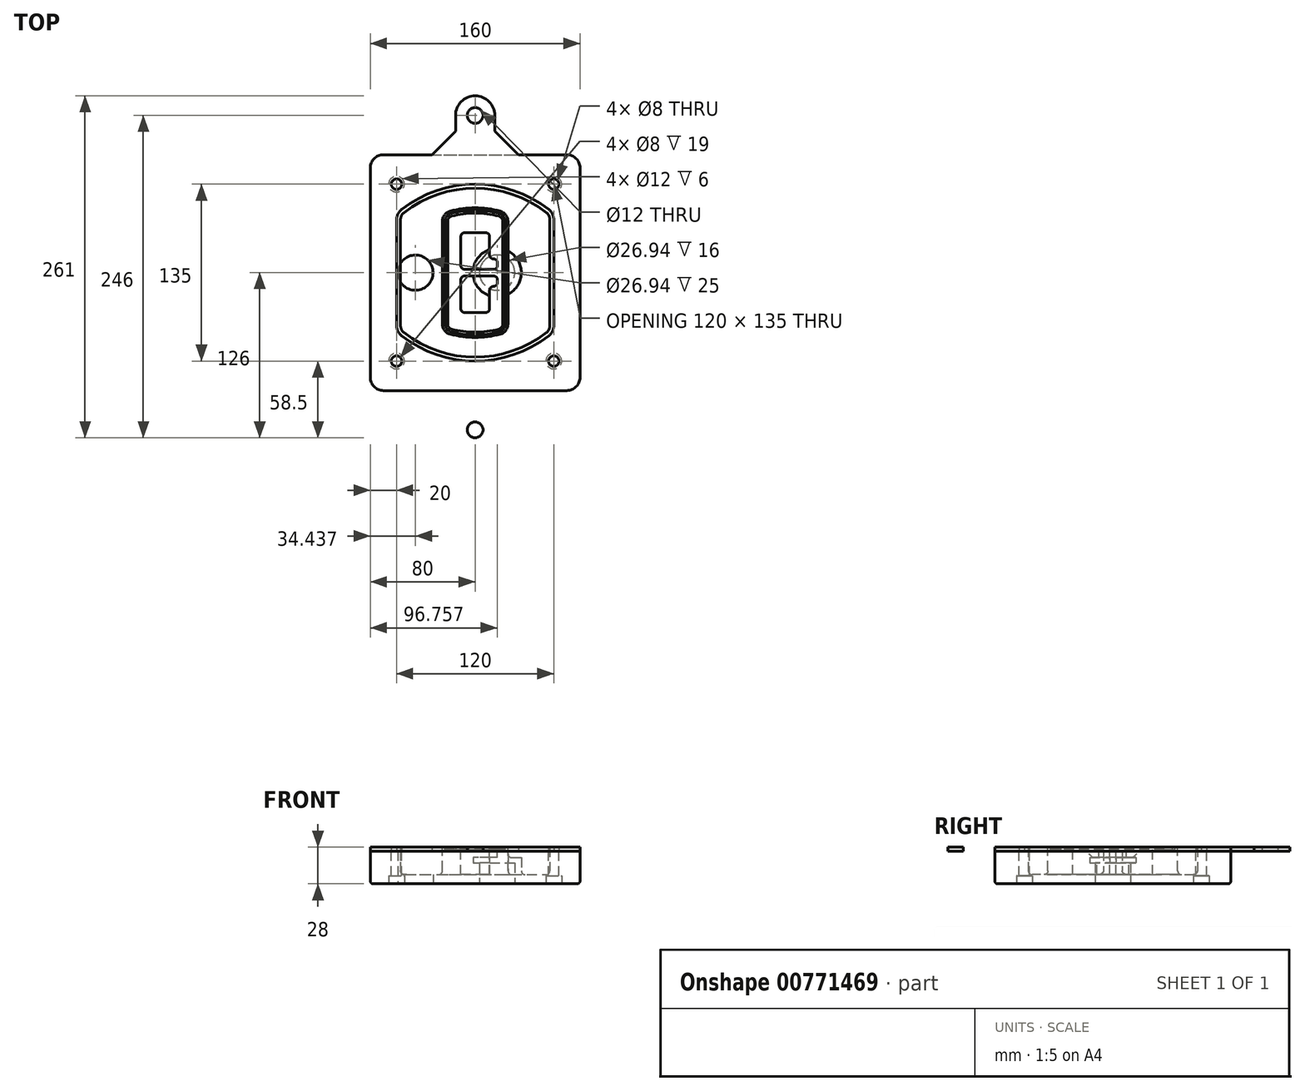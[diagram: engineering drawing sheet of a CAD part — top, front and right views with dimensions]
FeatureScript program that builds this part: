
annotation { "Feature Type Name" : "Feature", "Feature Type Description" : "" }
export const myFeature = defineFeature(function(context is Context, id is Id, definition is map)
    precondition{}
    {
        {
            var Q0;
            Q0=qCreatedBy(makeId("Top.planeOp"),FACE);
            var sketch = newSketch(context, id + "F0", { "sketchPlane" : qUnion([Q0])});
            skPoint(sketch, "E0.rect.middle", {"position": v(0, 0) * mm});
            skLineSegment(sketch, "E1.bottom", {"start": v(-70, -90) * mm, "end": v(70, -90) * mm});
            skLineSegment(sketch, "E1.top", {"start": v(-70, 90) * mm, "end": v(70, 90) * mm});
            skLineSegment(sketch, "E1.left", {"start": v(-80, -80) * mm, "end": v(-80, 80) * mm});
            skLineSegment(sketch, "E1.right", {"start": v(80, -80) * mm, "end": v(80, 80) * mm});
            skLineSegment(sketch, "E2", {"start": v(-80, 90) * mm, "end": v(80, -90) * mm, "construction": true});
            skLineSegment(sketch, "E3", {"start": v(80, 90) * mm, "end": v(-80, -90) * mm, "construction": true});
            skCircle(sketch, "E4", {"center": v(-60, 67.5) * mm, "radius": 4 * mm});
            skCircle(sketch, "E5", {"center": v(60, 67.5) * mm, "radius": 4 * mm});
            skCircle(sketch, "E6", {"center": v(60, -67.5) * mm, "radius": 4 * mm});
            skCircle(sketch, "E7", {"center": v(-60, -67.5) * mm, "radius": 4 * mm});
            skLineSegment(sketch, "E8", {"start": v(-60, 67.5) * mm, "end": v(60, 67.5) * mm, "construction": true});
            skLineSegment(sketch, "E9", {"start": v(60, 67.5) * mm, "end": v(60, -67.5) * mm, "construction": true});
            skLineSegment(sketch, "E10", {"start": v(60, -67.5) * mm, "end": v(-60, -67.5) * mm, "construction": true});
            skLineSegment(sketch, "E11", {"start": v(-60, -67.5) * mm, "end": v(-60, 67.5) * mm, "construction": true});
            skLineSegment(sketch, "E12", {"start": v(-60, 40.3) * mm, "end": v(-60, -40.3) * mm});
            skLineSegment(sketch, "E13", {"start": v(60, 40.3) * mm, "end": v(60, -40.3) * mm});
            skArc(sketch, "E14", {"start": v(56.15, 48.18) * mm, "mid": v(0, 67.5) * mm, "end": v(-56.15, 48.18) * mm});
            skArc(sketch, "E15", {"start": v(-56.15, -48.18) * mm, "mid": v(0, -67.5) * mm, "end": v(56.15, -48.18) * mm});
            skLineSegment(sketch, "E16", {"start": v(-60, 0) * mm, "end": v(60, 0) * mm, "construction": true});
            skPoint(sketch, "E17.visualSharp", {"position": v(-60, -45) * mm});
            skArc(sketch, "E17.filletArc", {"start": v(-60, -40.3) * mm, "mid": v(-58.99, -44.68) * mm, "end": v(-56.15, -48.18) * mm});
            skPoint(sketch, "E18.visualSharp", {"position": v(-60, 45) * mm});
            skArc(sketch, "E18.filletArc", {"start": v(-56.15, 48.18) * mm, "mid": v(-58.99, 44.68) * mm, "end": v(-60, 40.3) * mm});
            skPoint(sketch, "E19.visualSharp", {"position": v(60, 45) * mm});
            skArc(sketch, "E19.filletArc", {"start": v(60, 40.3) * mm, "mid": v(58.99, 44.68) * mm, "end": v(56.15, 48.18) * mm});
            skPoint(sketch, "E20.visualSharp", {"position": v(60, -45) * mm});
            skArc(sketch, "E20.filletArc", {"start": v(56.15, -48.18) * mm, "mid": v(58.99, -44.68) * mm, "end": v(60, -40.3) * mm});
            skPoint(sketch, "E21.visualSharp", {"position": v(-80, 90) * mm});
            skArc(sketch, "E21.filletArc", {"start": v(-70, 90) * mm, "mid": v(-77.07, 87.07) * mm, "end": v(-80, 80) * mm});
            skPoint(sketch, "E22.visualSharp", {"position": v(80, 90) * mm});
            skArc(sketch, "E22.filletArc", {"start": v(80, 80) * mm, "mid": v(77.07, 87.07) * mm, "end": v(70, 90) * mm});
            skPoint(sketch, "E23.visualSharp", {"position": v(80, -90) * mm});
            skArc(sketch, "E23.filletArc", {"start": v(70, -90) * mm, "mid": v(77.07, -87.07) * mm, "end": v(80, -80) * mm});
            skPoint(sketch, "E24.visualSharp", {"position": v(-80, -90) * mm});
            skArc(sketch, "E24.filletArc", {"start": v(-80, -80) * mm, "mid": v(-77.07, -87.07) * mm, "end": v(-70, -90) * mm});
            skArc(sketch, "E25.0", {"start": v(57, 40.3) * mm, "mid": v(56.3, 43.36) * mm, "end": v(54.3, 45.81) * mm});
            skLineSegment(sketch, "E25.1", {"start": v(57, 40.3) * mm, "end": v(57, -40.3) * mm});
            skArc(sketch, "E25.2", {"start": v(54.3, -45.81) * mm, "mid": v(56.3, -43.36) * mm, "end": v(57, -40.3) * mm});
            skArc(sketch, "E25.3", {"start": v(-54.3, -45.81) * mm, "mid": v(0, -64.5) * mm, "end": v(54.3, -45.81) * mm});
            skArc(sketch, "E25.4", {"start": v(-57, -40.3) * mm, "mid": v(-56.3, -43.36) * mm, "end": v(-54.3, -45.81) * mm});
            skArc(sketch, "E25.5", {"start": v(54.3, 45.81) * mm, "mid": v(0, 64.5) * mm, "end": v(-54.3, 45.81) * mm});
            skLineSegment(sketch, "E25.6", {"start": v(-57, 40.3) * mm, "end": v(-57, -40.3) * mm});
            skArc(sketch, "E25.7", {"start": v(-54.3, 45.81) * mm, "mid": v(-56.3, 43.36) * mm, "end": v(-57, 40.3) * mm});
            skArc(sketch, "E26.0", {"start": v(-58.62, 51.33) * mm, "mid": v(-62.58, 46.43) * mm, "end": v(-64, 40.3) * mm});
            skArc(sketch, "E26.1", {"start": v(58.62, 51.33) * mm, "mid": v(0, 71.5) * mm, "end": v(-58.62, 51.33) * mm});
            skArc(sketch, "E26.2", {"start": v(64, 40.3) * mm, "mid": v(62.58, 46.43) * mm, "end": v(58.62, 51.33) * mm});
            skLineSegment(sketch, "E26.3", {"start": v(64, 40.3) * mm, "end": v(64, -40.3) * mm});
            skArc(sketch, "E26.4", {"start": v(58.62, -51.33) * mm, "mid": v(62.58, -46.43) * mm, "end": v(64, -40.3) * mm});
            skLineSegment(sketch, "E26.5", {"start": v(-64, 40.3) * mm, "end": v(-64, -40.3) * mm});
            skArc(sketch, "E26.6", {"start": v(-58.62, -51.33) * mm, "mid": v(0, -71.5) * mm, "end": v(58.62, -51.33) * mm});
            skArc(sketch, "E26.7", {"start": v(-64, -40.3) * mm, "mid": v(-62.58, -46.43) * mm, "end": v(-58.62, -51.33) * mm});
            skSolve(sketch);
        }
        {
            var Q0;
            Q0=makeQuery(id+"F0.imprint","IMPRINT",FACE,{"disambiguationData":[TD([[makeQuery(id+"F0.imprint","IMPRINT",EDGE,{"derivedFrom":sQuery(id+"F0.wireOp",EDGE,"E1.bottom")}),1.0]])]});
            var Q1;
            Q1=makeQuery(id+"F0.imprint","IMPRINT",FACE,{"disambiguationData":[TD([[makeQuery(id+"F0.imprint","IMPRINT",EDGE,{"derivedFrom":sQuery(id+"F0.wireOp",EDGE,"E12")}),1.0]])]});
            var Q2;
            Q2=makeQuery(id+"F0.imprint","IMPRINT",FACE,{"disambiguationData":[TD([[makeQuery(id+"F0.imprint","IMPRINT",EDGE,{"derivedFrom":sQuery(id+"F0.wireOp",EDGE,"E25.0")}),1.0]])]});
            var Q3;
            Q3=makeQuery(id+"F0.imprint","IMPRINT",FACE,{"disambiguationData":[TD([[makeQuery(id+"F0.imprint","IMPRINT",EDGE,{"derivedFrom":sQuery(id+"F0.wireOp",EDGE,"E12")}),-1.0]])]});
            extrude(context, id + "F1", {"entities" : qUnion([Q0, Q1, Q2, Q3]), "oppositeDirection" : true, "depth" : 25 * mm});
        }
        {
            var Q0;
            Q0=makeQuery(id+"F0.imprint","IMPRINT",FACE,{"disambiguationData":[TD([[makeQuery(id+"F0.imprint","IMPRINT",EDGE,{"derivedFrom":sQuery(id+"F0.wireOp",EDGE,"E12")}),1.0]])]});
            extrude(context, id + "F2", {"entities" : qUnion([Q0]), "operationType" : NewBodyOperationType.ADD, "depth" : 3 * mm});
        }
        {
            var Q0;
            Q0=makeQuery(id+"F0.imprint","IMPRINT",FACE,{"disambiguationData":[TD([[makeQuery(id+"F0.imprint","IMPRINT",EDGE,{"derivedFrom":sQuery(id+"F0.wireOp",EDGE,"E25.0")}),1.0]])]});
            extrude(context, id + "F3", {"entities" : qUnion([Q0]), "operationType" : NewBodyOperationType.REMOVE, "oppositeDirection" : true, "depth" : 18 * mm});
        }
        {
            var Q0;
            Q0=makeQuery(id+"F2.opExtrude","CAP_FACE",FACE,{"disambiguationData":[OSD([sQuery(id+"F0.wireOp",EDGE,"E12"),sQuery(id+"F0.wireOp",EDGE,"E13"),sQuery(id+"F0.wireOp",EDGE,"E14"),sQuery(id+"F0.wireOp",EDGE,"E15"),sQuery(id+"F0.wireOp",EDGE,"E17.filletArc"),sQuery(id+"F0.wireOp",EDGE,"E18.filletArc"),sQuery(id+"F0.wireOp",EDGE,"E19.filletArc"),sQuery(id+"F0.wireOp",EDGE,"E20.filletArc"),sQuery(id+"F0.wireOp",EDGE,"E25.0"),sQuery(id+"F0.wireOp",EDGE,"E25.1"),sQuery(id+"F0.wireOp",EDGE,"E25.2"),sQuery(id+"F0.wireOp",EDGE,"E25.3"),sQuery(id+"F0.wireOp",EDGE,"E25.4"),sQuery(id+"F0.wireOp",EDGE,"E25.5"),sQuery(id+"F0.wireOp",EDGE,"E25.6"),sQuery(id+"F0.wireOp",EDGE,"E25.7")])],"isStart":false});
            var sketch = newSketch(context, id + "F4", { "sketchPlane" : qUnion([Q0])});
            skArc(sketch, "E27.0", {"start": v(-19.08, -46.97) * mm, "mid": v(0, -49.5) * mm, "end": v(19.08, -46.97) * mm});
            skArc(sketch, "E28.0", {"start": v(19.08, 46.97) * mm, "mid": v(0, 49.5) * mm, "end": v(-19.08, 46.97) * mm});
            skLineSegment(sketch, "E29", {"start": v(-25, 39.25) * mm, "end": v(-25, -39.25) * mm});
            skLineSegment(sketch, "E30", {"start": v(25, 39.25) * mm, "end": v(25, -39.25) * mm});
            skLineSegment(sketch, "E31", {"start": v(-25, 45.1) * mm, "end": v(25, 45.1) * mm, "construction": true});
            skLineSegment(sketch, "E32", {"start": v(-25, -45.1) * mm, "end": v(25, -45.1) * mm, "construction": true});
            skPoint(sketch, "E33.visualSharp", {"position": v(-25, 45.1) * mm});
            skArc(sketch, "E33.filletArc", {"start": v(-19.08, 46.97) * mm, "mid": v(-23.35, 44.11) * mm, "end": v(-25, 39.25) * mm});
            skPoint(sketch, "E34.visualSharp", {"position": v(25, 45.1) * mm});
            skArc(sketch, "E34.filletArc", {"start": v(25, 39.25) * mm, "mid": v(23.35, 44.11) * mm, "end": v(19.08, 46.97) * mm});
            skPoint(sketch, "E35.visualSharp", {"position": v(25, -45.1) * mm});
            skArc(sketch, "E35.filletArc", {"start": v(19.08, -46.97) * mm, "mid": v(23.35, -44.11) * mm, "end": v(25, -39.25) * mm});
            skPoint(sketch, "E36.visualSharp", {"position": v(-25, -45.1) * mm});
            skArc(sketch, "E36.filletArc", {"start": v(-25, -39.25) * mm, "mid": v(-23.35, -44.11) * mm, "end": v(-19.08, -46.97) * mm});
            skArc(sketch, "E37.0", {"start": v(54.3, 45.81) * mm, "mid": v(0, 64.5) * mm, "end": v(-54.3, 45.81) * mm});
            skArc(sketch, "E37.1", {"start": v(-54.3, 45.81) * mm, "mid": v(-56.3, 43.36) * mm, "end": v(-57, 40.3) * mm});
            skLineSegment(sketch, "E37.2", {"start": v(-57, 40.3) * mm, "end": v(-57, -40.3) * mm});
            skArc(sketch, "E37.3", {"start": v(-57, -40.3) * mm, "mid": v(-56.3, -43.36) * mm, "end": v(-54.3, -45.81) * mm});
            skArc(sketch, "E37.4", {"start": v(-54.3, -45.81) * mm, "mid": v(0, -64.5) * mm, "end": v(54.3, -45.81) * mm});
            skArc(sketch, "E37.5", {"start": v(54.3, -45.81) * mm, "mid": v(56.3, -43.36) * mm, "end": v(57, -40.3) * mm});
            skLineSegment(sketch, "E37.6", {"start": v(57, 40.3) * mm, "end": v(57, -40.3) * mm});
            skArc(sketch, "E37.7", {"start": v(57, 40.3) * mm, "mid": v(56.3, 43.36) * mm, "end": v(54.3, 45.81) * mm});
            skLineSegment(sketch, "E38.0", {"start": v(23, 39.25) * mm, "end": v(23, -39.25) * mm});
            skArc(sketch, "E38.1", {"start": v(18.56, -45.04) * mm, "mid": v(21.76, -42.9) * mm, "end": v(23, -39.25) * mm});
            skArc(sketch, "E38.2", {"start": v(-18.56, -45.04) * mm, "mid": v(0, -47.5) * mm, "end": v(18.56, -45.04) * mm});
            skArc(sketch, "E38.3", {"start": v(-23, -39.25) * mm, "mid": v(-21.76, -42.9) * mm, "end": v(-18.56, -45.04) * mm});
            skLineSegment(sketch, "E38.4", {"start": v(-23, 39.25) * mm, "end": v(-23, -39.25) * mm});
            skArc(sketch, "E38.5", {"start": v(23, 39.25) * mm, "mid": v(21.76, 42.9) * mm, "end": v(18.56, 45.04) * mm});
            skArc(sketch, "E38.6", {"start": v(-18.56, 45.04) * mm, "mid": v(-21.76, 42.9) * mm, "end": v(-23, 39.25) * mm});
            skArc(sketch, "E38.7", {"start": v(18.56, 45.04) * mm, "mid": v(0, 47.5) * mm, "end": v(-18.56, 45.04) * mm});
            skArc(sketch, "E39.0", {"start": v(21, 39.25) * mm, "mid": v(20.18, 41.68) * mm, "end": v(18.04, 43.1) * mm});
            skLineSegment(sketch, "E39.1", {"start": v(21, 39.25) * mm, "end": v(21, -39.25) * mm});
            skArc(sketch, "E39.2", {"start": v(18.04, -43.1) * mm, "mid": v(20.18, -41.68) * mm, "end": v(21, -39.25) * mm});
            skArc(sketch, "E39.3", {"start": v(-18.04, -43.1) * mm, "mid": v(0, -45.5) * mm, "end": v(18.04, -43.1) * mm});
            skArc(sketch, "E39.4", {"start": v(-21, -39.25) * mm, "mid": v(-20.18, -41.68) * mm, "end": v(-18.04, -43.1) * mm});
            skArc(sketch, "E39.5", {"start": v(18.04, 43.1) * mm, "mid": v(0, 45.5) * mm, "end": v(-18.04, 43.1) * mm});
            skLineSegment(sketch, "E39.6", {"start": v(-21, 39.25) * mm, "end": v(-21, -39.25) * mm});
            skArc(sketch, "E39.7", {"start": v(-18.04, 43.1) * mm, "mid": v(-20.18, 41.68) * mm, "end": v(-21, 39.25) * mm});
            skLineSegment(sketch, "E40", {"start": v(-25, 0) * mm, "end": v(25, 0) * mm, "construction": true});
            skLineSegment(sketch, "E41", {"start": v(-11, 5.5) * mm, "end": v(-11, 27.5) * mm});
            skLineSegment(sketch, "E42", {"start": v(-8, 30.5) * mm, "end": v(8, 30.5) * mm});
            skLineSegment(sketch, "E43", {"start": v(11, 27.5) * mm, "end": v(11, 13.5) * mm});
            skLineSegment(sketch, "E44", {"start": v(14, 10.5) * mm, "end": v(14, 10.5) * mm});
            skLineSegment(sketch, "E45", {"start": v(17, 7.5) * mm, "end": v(17, 5.5) * mm});
            skLineSegment(sketch, "E46", {"start": v(14, 2.5) * mm, "end": v(-8, 2.5) * mm});
            skPoint(sketch, "E47.visualSharp", {"position": v(-11, 30.5) * mm});
            skArc(sketch, "E47.filletArc", {"start": v(-8, 30.5) * mm, "mid": v(-10.12, 29.62) * mm, "end": v(-11, 27.5) * mm});
            skPoint(sketch, "E48.visualSharp", {"position": v(11, 30.5) * mm});
            skArc(sketch, "E48.filletArc", {"start": v(11, 27.5) * mm, "mid": v(10.12, 29.62) * mm, "end": v(8, 30.5) * mm});
            skPoint(sketch, "E49.visualSharp", {"position": v(11, 10.5) * mm});
            skArc(sketch, "E49.filletArc", {"start": v(11, 13.5) * mm, "mid": v(11.88, 11.38) * mm, "end": v(14, 10.5) * mm});
            skPoint(sketch, "E50.visualSharp", {"position": v(17, 10.5) * mm});
            skArc(sketch, "E50.filletArc", {"start": v(17, 7.5) * mm, "mid": v(16.12, 9.62) * mm, "end": v(14, 10.5) * mm});
            skPoint(sketch, "E51.visualSharp", {"position": v(17, 2.5) * mm});
            skArc(sketch, "E51.filletArc", {"start": v(14, 2.5) * mm, "mid": v(16.12, 3.38) * mm, "end": v(17, 5.5) * mm});
            skPoint(sketch, "E52.visualSharp", {"position": v(-11, 2.5) * mm});
            skArc(sketch, "E52.filletArc", {"start": v(-11, 5.5) * mm, "mid": v(-10.12, 3.38) * mm, "end": v(-8, 2.5) * mm});
            skLineSegment(sketch, "E53.0.MirrorCS", {"start": v(14, -2.5) * mm, "end": v(-8, -2.5) * mm});
            skArc(sketch, "E54.0.MirrorCS", {"start": v(-11, -5.5) * mm, "mid": v(-10.12, -3.38) * mm, "end": v(-8, -2.5) * mm});
            skLineSegment(sketch, "E55.0.MirrorCS", {"start": v(-11, -5.5) * mm, "end": v(-11, -27.5) * mm});
            skArc(sketch, "E56.0.MirrorCS", {"start": v(-8, -30.5) * mm, "mid": v(-10.12, -29.62) * mm, "end": v(-11, -27.5) * mm});
            skLineSegment(sketch, "E57.0.MirrorCS", {"start": v(-8, -30.5) * mm, "end": v(8, -30.5) * mm});
            skArc(sketch, "E58.0.MirrorCS", {"start": v(11, -27.5) * mm, "mid": v(10.12, -29.62) * mm, "end": v(8, -30.5) * mm});
            skLineSegment(sketch, "E59.0.MirrorCS", {"start": v(11, -27.5) * mm, "end": v(11, -13.5) * mm});
            skArc(sketch, "E60.0.MirrorCS", {"start": v(11, -13.5) * mm, "mid": v(11.88, -11.38) * mm, "end": v(14, -10.5) * mm});
            skArc(sketch, "E61.0.MirrorCS", {"start": v(17, -7.5) * mm, "mid": v(16.12, -9.62) * mm, "end": v(14, -10.5) * mm});
            skLineSegment(sketch, "E62.0.MirrorCS", {"start": v(17, -7.5) * mm, "end": v(17, -5.5) * mm});
            skArc(sketch, "E63.0.MirrorCS", {"start": v(14, -2.5) * mm, "mid": v(16.12, -3.38) * mm, "end": v(17, -5.5) * mm});
            skSolve(sketch);
        }
        {
            var Q0;
            Q0=makeQuery(id+"F4.imprint","IMPRINT",FACE,{"disambiguationData":[TD([[makeQuery(id+"F4.imprint","IMPRINT",EDGE,{"derivedFrom":sQuery(id+"F4.wireOp",EDGE,"E27.0")}),1.0]])]});
            var Q1;
            Q1=makeQuery(id+"F4.imprint","IMPRINT",FACE,{"disambiguationData":[TD([[makeQuery(id+"F4.imprint","IMPRINT",EDGE,{"derivedFrom":sQuery(id+"F4.wireOp",EDGE,"E38.0")}),-1.0]])]});
            var Q2;
            Q2=makeQuery(id+"F4.imprint","IMPRINT",FACE,{"disambiguationData":[TD([[makeQuery(id+"F4.imprint","IMPRINT",EDGE,{"derivedFrom":sQuery(id+"F4.wireOp",EDGE,"E39.0")}),1.0]])]});
            extrude(context, id + "F5", {"entities" : qUnion([Q0, Q1, Q2]), "operationType" : NewBodyOperationType.ADD, "endBound" : BoundingType.UP_TO_NEXT, "oppositeDirection" : true, "depth" : 25 * mm});
        }
        {
            var Q0;
            Q0=makeQuery(id+"F4.imprint","IMPRINT",FACE,{"disambiguationData":[TD([[makeQuery(id+"F4.imprint","IMPRINT",EDGE,{"derivedFrom":sQuery(id+"F4.wireOp",EDGE,"E38.0")}),-1.0]])]});
            extrude(context, id + "F6", {"entities" : qUnion([Q0]), "operationType" : NewBodyOperationType.REMOVE, "oppositeDirection" : true, "depth" : 2 * mm});
        }
        {
            var Q0;
            Q0=makeQuery(id+"F1.opExtrude","CAP_FACE",FACE,{"disambiguationData":[OSD([sQuery(id+"F0.wireOp",EDGE,"E1.bottom"),sQuery(id+"F0.wireOp",EDGE,"E1.top"),sQuery(id+"F0.wireOp",EDGE,"E1.left"),sQuery(id+"F0.wireOp",EDGE,"E1.right"),sQuery(id+"F0.wireOp",EDGE,"E4"),sQuery(id+"F0.wireOp",EDGE,"E5"),sQuery(id+"F0.wireOp",EDGE,"E6"),sQuery(id+"F0.wireOp",EDGE,"E7"),sQuery(id+"F0.wireOp",EDGE,"E21.filletArc"),sQuery(id+"F0.wireOp",EDGE,"E22.filletArc"),sQuery(id+"F0.wireOp",EDGE,"E23.filletArc"),sQuery(id+"F0.wireOp",EDGE,"E24.filletArc")])],"isStart":false});
            var sketch = newSketch(context, id + "F7", { "sketchPlane" : qUnion([Q0])});
            skCircle(sketch, "E64", {"center": v(16.76, 0) * mm, "radius": 13.47 * mm});
            skCircle(sketch, "E65", {"center": v(-45.56, 0) * mm, "radius": 13.47 * mm});
            skLineSegment(sketch, "E66", {"start": v(80, 0) * mm, "end": v(-80, 0) * mm});
            skCircle(sketch, "E67", {"center": v(16.76, 0) * mm, "radius": 18.47 * mm});
            skCircle(sketch, "E68", {"center": v(60, -67.5) * mm, "radius": 6 * mm});
            skCircle(sketch, "E69", {"center": v(-60, -67.5) * mm, "radius": 6 * mm});
            skCircle(sketch, "E70", {"center": v(-60, 67.5) * mm, "radius": 6 * mm});
            skCircle(sketch, "E71", {"center": v(60, 67.5) * mm, "radius": 6 * mm});
            skSolve(sketch);
        }
        {
            var Q0;
            {var subQ1=sQuery(id+"F7.wireOp",EDGE,"E66");var subQ4=sQuery(id+"F7.wireOp",EDGE,"E64");var subQ6=makeQuery(id+"F7.imprint","INTERSECT",VERTEX,{"disambiguationData":[OD(0.0)],"derivedFrom":[subQ4,subQ1]});Q0=makeQuery(id+"F7.imprint","IMPRINT",FACE,{"disambiguationData":[TD([[makeQuery(id+"F7.imprint","IMPRINT",EDGE,{"disambiguationData":[TD([[subQ6,-1.0]])],"derivedFrom":subQ4}),-1.0]])]});}
            var Q1;
            {var subQ0=sQuery(id+"F7.wireOp",EDGE,"E66");var subQ1=sQuery(id+"F7.wireOp",EDGE,"E64");var subQ3=makeQuery(id+"F7.imprint","INTERSECT",VERTEX,{"disambiguationData":[OD(0.0)],"derivedFrom":[subQ1,subQ0]});Q1=makeQuery(id+"F7.imprint","IMPRINT",FACE,{"disambiguationData":[TD([[makeQuery(id+"F7.imprint","IMPRINT",EDGE,{"disambiguationData":[TD([[subQ3,-1.0]])],"derivedFrom":subQ1}),1.0]])]});}
            var Q2;
            {var subQ0=sQuery(id+"F7.wireOp",EDGE,"E66");var subQ1=sQuery(id+"F7.wireOp",EDGE,"E64");var subQ3=makeQuery(id+"F7.imprint","INTERSECT",VERTEX,{"disambiguationData":[OD(0.0)],"derivedFrom":[subQ1,subQ0]});Q2=makeQuery(id+"F7.imprint","IMPRINT",FACE,{"disambiguationData":[TD([[makeQuery(id+"F7.imprint","IMPRINT",EDGE,{"disambiguationData":[TD([[subQ3,1.0]])],"derivedFrom":subQ1}),1.0]])]});}
            var Q3;
            {var subQ1=sQuery(id+"F7.wireOp",EDGE,"E66");var subQ4=sQuery(id+"F7.wireOp",EDGE,"E64");var subQ6=makeQuery(id+"F7.imprint","INTERSECT",VERTEX,{"disambiguationData":[OD(0.0)],"derivedFrom":[subQ4,subQ1]});Q3=makeQuery(id+"F7.imprint","IMPRINT",FACE,{"disambiguationData":[TD([[makeQuery(id+"F7.imprint","IMPRINT",EDGE,{"disambiguationData":[TD([[subQ6,1.0]])],"derivedFrom":subQ4}),-1.0]])]});}
            extrude(context, id + "F8", {"entities" : qUnion([Q0, Q1, Q2, Q3]), "operationType" : NewBodyOperationType.ADD, "oppositeDirection" : true, "depth" : 20 * mm});
        }
        {
            var Q0;
            {var subQ0=sQuery(id+"F7.wireOp",EDGE,"E66");var subQ1=sQuery(id+"F7.wireOp",EDGE,"E64");var subQ3=makeQuery(id+"F7.imprint","INTERSECT",VERTEX,{"disambiguationData":[OD(0.0)],"derivedFrom":[subQ1,subQ0]});Q0=makeQuery(id+"F7.imprint","IMPRINT",FACE,{"disambiguationData":[TD([[makeQuery(id+"F7.imprint","IMPRINT",EDGE,{"disambiguationData":[TD([[subQ3,-1.0]])],"derivedFrom":subQ1}),1.0]])]});}
            var Q1;
            {var subQ0=sQuery(id+"F7.wireOp",EDGE,"E66");var subQ1=sQuery(id+"F7.wireOp",EDGE,"E64");var subQ3=makeQuery(id+"F7.imprint","INTERSECT",VERTEX,{"disambiguationData":[OD(0.0)],"derivedFrom":[subQ1,subQ0]});Q1=makeQuery(id+"F7.imprint","IMPRINT",FACE,{"disambiguationData":[TD([[makeQuery(id+"F7.imprint","IMPRINT",EDGE,{"disambiguationData":[TD([[subQ3,1.0]])],"derivedFrom":subQ1}),1.0]])]});}
            extrude(context, id + "F9", {"entities" : qUnion([Q0, Q1]), "operationType" : NewBodyOperationType.REMOVE, "oppositeDirection" : true, "depth" : 16 * mm});
        }
        {
            var Q0;
            {var subQ0=sQuery(id+"F7.wireOp",EDGE,"E66");var subQ1=sQuery(id+"F7.wireOp",EDGE,"E65");var subQ3=makeQuery(id+"F7.imprint","INTERSECT",VERTEX,{"disambiguationData":[OD(0.0)],"derivedFrom":[subQ1,subQ0]});Q0=makeQuery(id+"F7.imprint","IMPRINT",FACE,{"disambiguationData":[TD([[makeQuery(id+"F7.imprint","IMPRINT",EDGE,{"disambiguationData":[TD([[subQ3,-1.0]])],"derivedFrom":subQ1}),1.0]])]});}
            var Q1;
            {var subQ0=sQuery(id+"F7.wireOp",EDGE,"E66");var subQ1=sQuery(id+"F7.wireOp",EDGE,"E65");var subQ3=makeQuery(id+"F7.imprint","INTERSECT",VERTEX,{"disambiguationData":[OD(0.0)],"derivedFrom":[subQ1,subQ0]});Q1=makeQuery(id+"F7.imprint","IMPRINT",FACE,{"disambiguationData":[TD([[makeQuery(id+"F7.imprint","IMPRINT",EDGE,{"disambiguationData":[TD([[subQ3,1.0]])],"derivedFrom":subQ1}),1.0]])]});}
            extrude(context, id + "F10", {"entities" : qUnion([Q0, Q1]), "operationType" : NewBodyOperationType.REMOVE, "oppositeDirection" : true, "depth" : 25 * mm});
        }
        {
            var Q0;
            Q0=makeQuery(id+"F7.imprint","IMPRINT",FACE,{"disambiguationData":[TD([[makeQuery(id+"F7.imprint","IMPRINT",EDGE,{"derivedFrom":sQuery(id+"F7.wireOp",EDGE,"E68")}),1.0]])]});
            var Q1;
            Q1=makeQuery(id+"F7.imprint","IMPRINT",FACE,{"disambiguationData":[TD([[makeQuery(id+"F7.imprint","IMPRINT",EDGE,{"derivedFrom":makeQuery(id+"F1.opExtrude","CAP_EDGE",EDGE,{"disambiguationData":[OSD([sQuery(id+"F0.wireOp",EDGE,"E5")])],"isStart":false})}),-1.0]])]});
            var Q2;
            Q2=makeQuery(id+"F7.imprint","IMPRINT",FACE,{"disambiguationData":[TD([[makeQuery(id+"F7.imprint","IMPRINT",EDGE,{"derivedFrom":sQuery(id+"F7.wireOp",EDGE,"E69")}),1.0]])]});
            var Q3;
            Q3=makeQuery(id+"F7.imprint","IMPRINT",FACE,{"disambiguationData":[TD([[makeQuery(id+"F7.imprint","IMPRINT",EDGE,{"derivedFrom":makeQuery(id+"F1.opExtrude","CAP_EDGE",EDGE,{"disambiguationData":[OSD([sQuery(id+"F0.wireOp",EDGE,"E4")])],"isStart":false})}),-1.0]])]});
            var Q4;
            Q4=makeQuery(id+"F7.imprint","IMPRINT",FACE,{"disambiguationData":[TD([[makeQuery(id+"F7.imprint","IMPRINT",EDGE,{"derivedFrom":sQuery(id+"F7.wireOp",EDGE,"E70")}),1.0]])]});
            var Q5;
            Q5=makeQuery(id+"F7.imprint","IMPRINT",FACE,{"disambiguationData":[TD([[makeQuery(id+"F7.imprint","IMPRINT",EDGE,{"derivedFrom":makeQuery(id+"F1.opExtrude","CAP_EDGE",EDGE,{"disambiguationData":[OSD([sQuery(id+"F0.wireOp",EDGE,"E7")])],"isStart":false})}),-1.0]])]});
            var Q6;
            Q6=makeQuery(id+"F7.imprint","IMPRINT",FACE,{"disambiguationData":[TD([[makeQuery(id+"F7.imprint","IMPRINT",EDGE,{"derivedFrom":sQuery(id+"F7.wireOp",EDGE,"E71")}),1.0]])]});
            var Q7;
            Q7=makeQuery(id+"F7.imprint","IMPRINT",FACE,{"disambiguationData":[TD([[makeQuery(id+"F7.imprint","IMPRINT",EDGE,{"derivedFrom":makeQuery(id+"F1.opExtrude","CAP_EDGE",EDGE,{"disambiguationData":[OSD([sQuery(id+"F0.wireOp",EDGE,"E6")])],"isStart":false})}),-1.0]])]});
            extrude(context, id + "F11", {"entities" : qUnion([Q0, Q1, Q2, Q3, Q4, Q5, Q6, Q7]), "operationType" : NewBodyOperationType.REMOVE, "oppositeDirection" : true, "depth" : 6 * mm});
        }
        {
            var Q0;
            Q0=makeQuery(id+"F9.boolean.opBoolean","COPY",FACE,{"derivedFrom":makeQuery(id+"F9.opExtrude","CAP_FACE",FACE,{"disambiguationData":[OSD([sQuery(id+"F7.wireOp",EDGE,"E64")])],"isStart":false})});
            var sketch = newSketch(context, id + "F12", { "sketchPlane" : qUnion([Q0])});
            skArc(sketch, "E72.0", {"start": v(11, 17.55) * mm, "mid": v(2.57, 11.82) * mm, "end": v(-1.54, 2.5) * mm});
            skArc(sketch, "E72.1", {"start": v(-1.54, -2.5) * mm, "mid": v(2.57, -11.82) * mm, "end": v(11, -17.55) * mm});
            skLineSegment(sketch, "E73", {"start": v(-1.54, -2.5) * mm, "end": v(14, -2.5) * mm});
            skLineSegment(sketch, "E74.0", {"start": v(14, 2.5) * mm, "end": v(-1.54, 2.5) * mm});
            skArc(sketch, "E74.1", {"start": v(14, 2.5) * mm, "mid": v(16.12, 3.38) * mm, "end": v(17, 5.5) * mm});
            skLineSegment(sketch, "E74.2", {"start": v(17, 7.5) * mm, "end": v(17, 5.5) * mm});
            skArc(sketch, "E74.3", {"start": v(17, 7.5) * mm, "mid": v(16.12, 9.62) * mm, "end": v(14, 10.5) * mm});
            skArc(sketch, "E74.4", {"start": v(11, 13.5) * mm, "mid": v(11.88, 11.38) * mm, "end": v(14, 10.5) * mm});
            skLineSegment(sketch, "E74.5", {"start": v(11, 17.55) * mm, "end": v(11, 13.5) * mm});
            skLineSegment(sketch, "E74.7", {"start": v(14, -2.5) * mm, "end": v(-1.54, -2.5) * mm});
            skArc(sketch, "E74.8", {"start": v(14, -2.5) * mm, "mid": v(16.12, -3.38) * mm, "end": v(17, -5.5) * mm});
            skLineSegment(sketch, "E74.9", {"start": v(17, -7.5) * mm, "end": v(17, -5.5) * mm});
            skArc(sketch, "E74.10", {"start": v(17, -7.5) * mm, "mid": v(16.12, -9.62) * mm, "end": v(14, -10.5) * mm});
            skArc(sketch, "E74.11", {"start": v(11, -13.5) * mm, "mid": v(11.88, -11.38) * mm, "end": v(14, -10.5) * mm});
            skLineSegment(sketch, "E74.12", {"start": v(11, -17.55) * mm, "end": v(11, -13.5) * mm});
            skPoint(sketch, "E75.orphan", {"position": v(11, -27.5) * mm});
            skPoint(sketch, "E76.orphan", {"position": v(-8, -2.5) * mm});
            skPoint(sketch, "E77.orphan", {"position": v(-8, 2.5) * mm});
            skPoint(sketch, "E78.orphan", {"position": v(11, 27.5) * mm});
            skSolve(sketch);
        }
        {
            var Q0;
            {var subQ7=sQuery(id+"F12.wireOp",EDGE,"E72.0");var subQ14=sQuery(id+"F12.wireOp",EDGE,"E72.1");var subQ16=sQuery(id+"F12.wireOp",EDGE,"E74.1");var subQ18=sQuery(id+"F12.wireOp",EDGE,"E74.8");Q0=qUnion([makeQuery(id+"F12.imprint","IMPRINT",FACE,{"disambiguationData":[TD([[makeQuery(id+"F12.imprint","IMPRINT",EDGE,{"derivedFrom":subQ7}),1.0]])]}),makeQuery(id+"F12.imprint","IMPRINT",FACE,{"disambiguationData":[TD([[makeQuery(id+"F12.imprint","IMPRINT",EDGE,{"derivedFrom":subQ14}),1.0]])]}),makeQuery(id+"F12.imprint","IMPRINT",FACE,{"disambiguationData":[TD([[makeQuery(id+"F12.imprint","IMPRINT",EDGE,{"derivedFrom":subQ16}),1.0]])]}),makeQuery(id+"F12.imprint","IMPRINT",FACE,{"disambiguationData":[TD([[makeQuery(id+"F12.imprint","IMPRINT",EDGE,{"derivedFrom":subQ18}),-1.0]])]})]);}
            var Q1;
            Q1=makeQuery(id+"F5.boolean.opBoolean","SPLIT",FACE,{"disambiguationData":[TD([makeQuery(id+"F5.opExtrude","SWEPT_FACE",FACE,{"disambiguationData":[OSD([sQuery(id+"F4.wireOp",EDGE,"E41")])]})])],"derivedFrom":makeQuery(id+"F3.boolean.opBoolean","COPY",FACE,{"derivedFrom":makeQuery(id+"F3.opExtrude","CAP_FACE",FACE,{"disambiguationData":[OSD([sQuery(id+"F0.wireOp",EDGE,"E25.0"),sQuery(id+"F0.wireOp",EDGE,"E25.1"),sQuery(id+"F0.wireOp",EDGE,"E25.2"),sQuery(id+"F0.wireOp",EDGE,"E25.3"),sQuery(id+"F0.wireOp",EDGE,"E25.4"),sQuery(id+"F0.wireOp",EDGE,"E25.5"),sQuery(id+"F0.wireOp",EDGE,"E25.6"),sQuery(id+"F0.wireOp",EDGE,"E25.7")])],"isStart":false})})});
            extrude(context, id + "F13", {"entities" : qUnion([Q0]), "operationType" : NewBodyOperationType.REMOVE, "endBound" : BoundingType.UP_TO_SURFACE, "endBoundEntityFace" : qUnion([Q1]), "depth" : 25 * mm});
        }
        {
            var Q0;
            Q0=makeQuery(id+"F3.boolean.opBoolean","COPY",EDGE,{"derivedFrom":makeQuery(id+"F3.opExtrude","CAP_EDGE",EDGE,{"disambiguationData":[OSD([sQuery(id+"F0.wireOp",EDGE,"E25.6")])],"isStart":false})});
            var Q1;
            Q1=makeQuery(id+"F8.boolean.opBoolean","INTERSECT",EDGE,{"derivedFrom":[makeQuery(id+"F5.opExtrude","SWEPT_FACE",FACE,{"disambiguationData":[OSD([sQuery(id+"F4.wireOp",EDGE,"E30")])]}),makeQuery(id+"F8.opExtrude","CAP_FACE",FACE,{"disambiguationData":[OSD([sQuery(id+"F7.wireOp",EDGE,"E67")])],"isStart":false})]});
            var Q2;
            Q2=makeQuery(id+"F8.boolean.opBoolean","INTERSECT",EDGE,{"disambiguationData":[OD(1.0)],"derivedFrom":[makeQuery(id+"F5.opExtrude","SWEPT_FACE",FACE,{"disambiguationData":[OSD([sQuery(id+"F4.wireOp",EDGE,"E30")])]}),makeQuery(id+"F8.opExtrude","SWEPT_FACE",FACE,{"disambiguationData":[OSD([sQuery(id+"F7.wireOp",EDGE,"E67")])]})]});
            var Q3;
            {var subQ0=sQuery(id+"F4.wireOp",EDGE,"E30");Q3=makeQuery(id+"F8.boolean.opBoolean","SPLIT",EDGE,{"disambiguationData":[TD([makeQuery(id+"F5.opExtrude","SWEPT_FACE",FACE,{"disambiguationData":[OSD([sQuery(id+"F4.wireOp",EDGE,"E35.filletArc")])]})])],"derivedFrom":makeQuery(id+"F5.opExtrude","CAP_EDGE",EDGE,{"disambiguationData":[OSD([subQ0])],"isStart":false})});}
            var Q4;
            {var subQ0=sQuery(id+"F0.wireOp",EDGE,"E25.7");var subQ1=sQuery(id+"F0.wireOp",EDGE,"E25.1");var subQ2=sQuery(id+"F0.wireOp",EDGE,"E25.6");var subQ3=sQuery(id+"F0.wireOp",EDGE,"E25.5");var subQ4=sQuery(id+"F0.wireOp",EDGE,"E25.4");var subQ5=sQuery(id+"F0.wireOp",EDGE,"E25.0");var subQ6=sQuery(id+"F0.wireOp",EDGE,"E25.2");var subQ7=sQuery(id+"F0.wireOp",EDGE,"E25.3");Q4=makeQuery(id+"F8.boolean.opBoolean","INTERSECT",EDGE,{"derivedFrom":[makeQuery(id+"F5.boolean.opBoolean","SPLIT",FACE,{"disambiguationData":[TD([makeQuery(id+"F2.opExtrude","SWEPT_FACE",FACE,{"disambiguationData":[OSD([subQ5])]})])],"derivedFrom":makeQuery(id+"F3.boolean.opBoolean","COPY",FACE,{"derivedFrom":makeQuery(id+"F3.opExtrude","CAP_FACE",FACE,{"disambiguationData":[OSD([subQ5,subQ1,subQ6,subQ7,subQ4,subQ3,subQ2,subQ0])],"isStart":false})})}),makeQuery(id+"F8.opExtrude","SWEPT_FACE",FACE,{"disambiguationData":[OSD([sQuery(id+"F7.wireOp",EDGE,"E67")])]})]});}
            var Q5;
            Q5=makeQuery(id+"F8.boolean.opBoolean","INTERSECT",EDGE,{"disambiguationData":[OD(0.0)],"derivedFrom":[makeQuery(id+"F5.opExtrude","SWEPT_FACE",FACE,{"disambiguationData":[OSD([sQuery(id+"F4.wireOp",EDGE,"E30")])]}),makeQuery(id+"F8.opExtrude","SWEPT_FACE",FACE,{"disambiguationData":[OSD([sQuery(id+"F7.wireOp",EDGE,"E67")])]})]});
            fillet(context, id + "F14", {"entities" : qUnion([Q0, Q1, Q2, Q3, Q4, Q5]), "radius" : 3 * mm, "tangentPropagation" : true, "allowEdgeOverflow" : false});
        }
        {
            var Q0;
            Q0=makeQuery(id+"F1.opExtrude","CAP_EDGE",EDGE,{"disambiguationData":[OSD([sQuery(id+"F0.wireOp",EDGE,"E1.bottom")])],"isStart":false});
            fillet(context, id + "F15", {"entities" : qUnion([Q0]), "radius" : 2 * mm, "tangentPropagation" : true, "allowEdgeOverflow" : false});
        }
        {
            var Q0;
            {var subQ0=sQuery(id+"F0.wireOp",EDGE,"E21.filletArc");var subQ1=sQuery(id+"F0.wireOp",EDGE,"E7");var subQ2=sQuery(id+"F0.wireOp",EDGE,"E6");var subQ3=sQuery(id+"F0.wireOp",EDGE,"E5");var subQ4=sQuery(id+"F0.wireOp",EDGE,"E4");var subQ5=sQuery(id+"F0.wireOp",EDGE,"E22.filletArc");var subQ6=sQuery(id+"F0.wireOp",EDGE,"E1.bottom");var subQ7=sQuery(id+"F0.wireOp",EDGE,"E1.right");var subQ8=sQuery(id+"F0.wireOp",EDGE,"E1.top");var subQ9=sQuery(id+"F0.wireOp",EDGE,"E1.left");var subQ10=sQuery(id+"F0.wireOp",EDGE,"E23.filletArc");var subQ11=sQuery(id+"F0.wireOp",EDGE,"E24.filletArc");Q0=makeQuery(id+"F2.boolean.opBoolean","SPLIT",FACE,{"disambiguationData":[TD([makeQuery(id+"F1.opExtrude","SWEPT_FACE",FACE,{"disambiguationData":[OSD([subQ6])]})])],"derivedFrom":makeQuery(id+"F1.opExtrude","CAP_FACE",FACE,{"disambiguationData":[OSD([subQ6,subQ8,subQ9,subQ7,subQ4,subQ3,subQ2,subQ1,subQ0,subQ5,subQ10,subQ11])],"isStart":true})});}
            var sketch = newSketch(context, id + "F16", { "sketchPlane" : qUnion([Q0])});
            skLineSegment(sketch, "E79", {"start": v(0, 90) * mm, "end": v(0, 120) * mm, "construction": true});
            skCircle(sketch, "E80", {"center": v(0, 120) * mm, "radius": 6 * mm});
            skLineSegment(sketch, "E81", {"start": v(-15, 120) * mm, "end": v(-15, 108) * mm});
            skLineSegment(sketch, "E82", {"start": v(15, 120) * mm, "end": v(15, 108) * mm});
            skLineSegment(sketch, "E83", {"start": v(15, 108) * mm, "end": v(33, 90) * mm});
            skLineSegment(sketch, "E84", {"start": v(-15, 108) * mm, "end": v(-33, 90) * mm});
            skArc(sketch, "E85", {"start": v(15, 120) * mm, "mid": v(0, 135) * mm, "end": v(-15, 120) * mm});
            skLineSegment(sketch, "E86", {"start": v(-80, 0) * mm, "end": v(80, 0) * mm, "construction": true});
            skLineSegment(sketch, "E87.MirrorCS", {"start": v(0, -90) * mm, "end": v(0, -120) * mm, "construction": true});
            skCircle(sketch, "E88.MirrorC", {"center": v(0, -120) * mm, "radius": 6 * mm});
            skLineSegment(sketch, "E89.MirrorCS", {"start": v(-15, -120) * mm, "end": v(-15, -108) * mm});
            skLineSegment(sketch, "E90.MirrorCS", {"start": v(15, -120) * mm, "end": v(15, -108) * mm});
            skLineSegment(sketch, "E91.MirrorCS", {"start": v(15, -108) * mm, "end": v(33, -90) * mm});
            skLineSegment(sketch, "E92.MirrorCS", {"start": v(-15, -108) * mm, "end": v(-33, -90) * mm});
            skArc(sketch, "E93.MirrorCS", {"start": v(15, -120) * mm, "mid": v(0, -135) * mm, "end": v(-15, -120) * mm});
            skSolve(sketch);
        }
        {
            var Q0;
            Q0=makeQuery(id+"F16.imprint","IMPRINT",FACE,{"disambiguationData":[TD([[makeQuery(id+"F16.imprint","IMPRINT",EDGE,{"derivedFrom":sQuery(id+"F16.wireOp",EDGE,"E80")}),-1.0]])]});
            var Q1;
            Q1=makeQuery(id+"F16.imprint","IMPRINT",FACE,{"disambiguationData":[TD([[makeQuery(id+"F16.imprint","IMPRINT",EDGE,{"derivedFrom":makeQuery(id+"F1.opExtrude","CAP_EDGE",EDGE,{"disambiguationData":[OSD([sQuery(id+"F0.wireOp",EDGE,"E1.left")])],"isStart":true})}),-1.0]])]});
            var Q2;
            Q2=makeQuery(id+"F16.imprint","IMPRINT",FACE,{"disambiguationData":[TD([[makeQuery(id+"F16.imprint","IMPRINT",EDGE,{"derivedFrom":sQuery(id+"F16.wireOp",EDGE,"E88.MirrorC")}),1.0]])]});
            var Q3;
            Q3=makeQuery(id+"F2.opExtrude","CAP_FACE",FACE,{"disambiguationData":[OSD([sQuery(id+"F0.wireOp",EDGE,"E12"),sQuery(id+"F0.wireOp",EDGE,"E13"),sQuery(id+"F0.wireOp",EDGE,"E14"),sQuery(id+"F0.wireOp",EDGE,"E15"),sQuery(id+"F0.wireOp",EDGE,"E17.filletArc"),sQuery(id+"F0.wireOp",EDGE,"E18.filletArc"),sQuery(id+"F0.wireOp",EDGE,"E19.filletArc"),sQuery(id+"F0.wireOp",EDGE,"E20.filletArc"),sQuery(id+"F0.wireOp",EDGE,"E25.0"),sQuery(id+"F0.wireOp",EDGE,"E25.1"),sQuery(id+"F0.wireOp",EDGE,"E25.2"),sQuery(id+"F0.wireOp",EDGE,"E25.3"),sQuery(id+"F0.wireOp",EDGE,"E25.4"),sQuery(id+"F0.wireOp",EDGE,"E25.5"),sQuery(id+"F0.wireOp",EDGE,"E25.6"),sQuery(id+"F0.wireOp",EDGE,"E25.7")])],"isStart":false});
            extrude(context, id + "F17", {"entities" : qUnion([Q0, Q1, Q2]), "endBound" : BoundingType.UP_TO_SURFACE, "depth" : 25 * mm, "endBoundEntityFace" : qUnion([Q3]), "offsetDistance" : 25 * mm});
        }
    });
